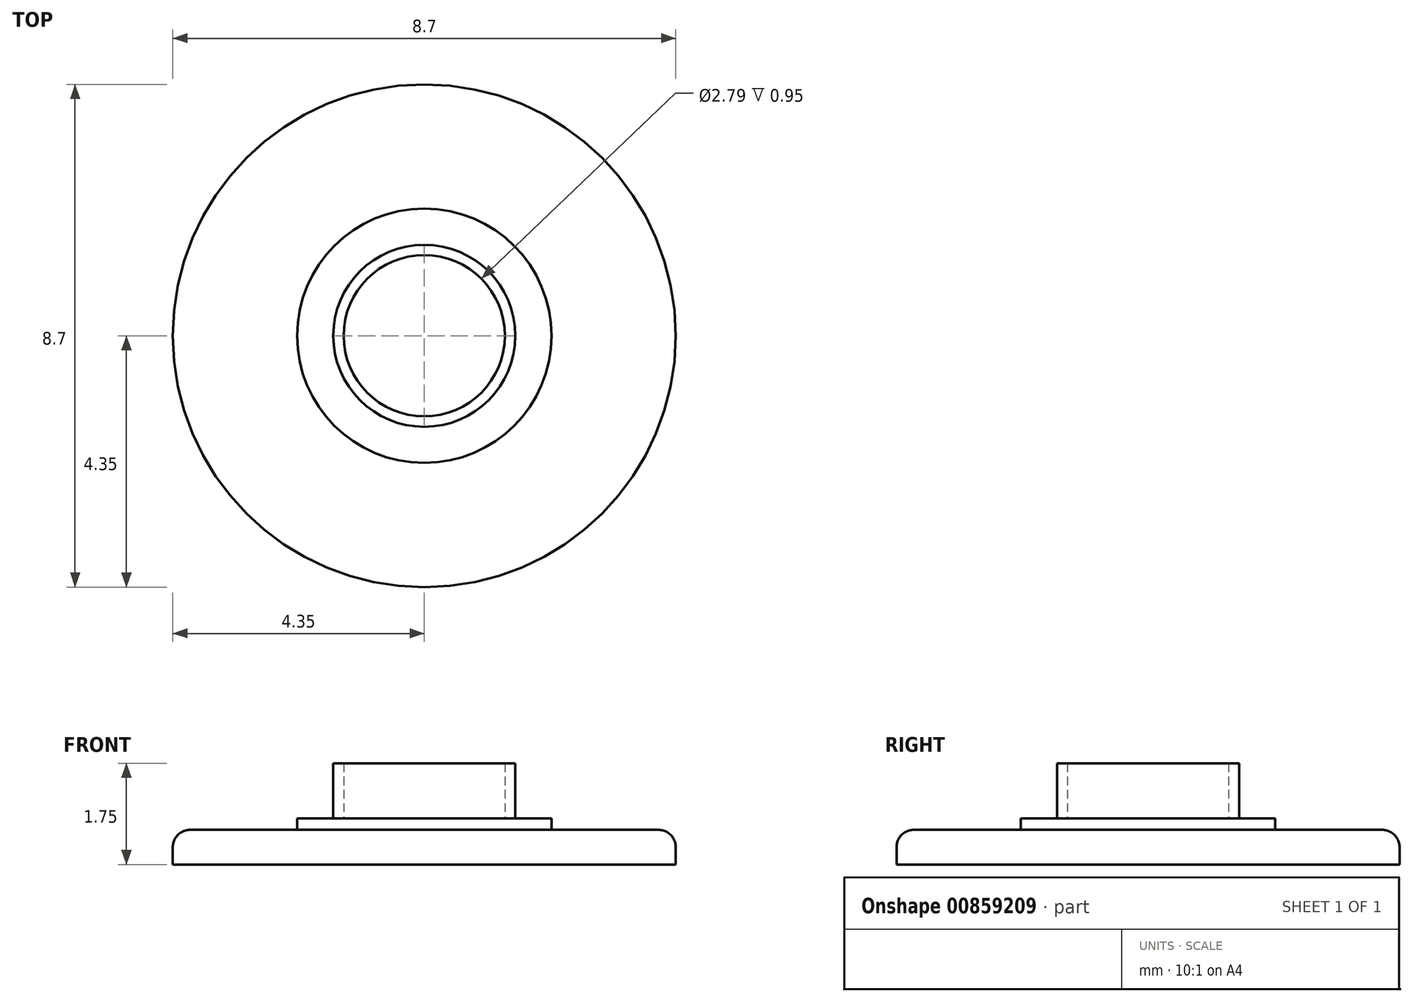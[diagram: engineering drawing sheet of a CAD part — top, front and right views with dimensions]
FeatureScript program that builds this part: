
annotation { "Feature Type Name" : "Feature", "Feature Type Description" : "" }
export const myFeature = defineFeature(function(context is Context, id is Id, definition is map)
    precondition{}
    {
        {
            var Q0;
            Q0=qCreatedBy(makeId("Top.planeOp"),FACE);
            var sketch = newSketch(context, id + "F0", { "sketchPlane" : qUnion([Q0])});
            skCircle(sketch, "E0", {"center": v(0, 0) * mm, "radius": 4.35 * mm});
            skSolve(sketch);
        }
        {
            var Q0;
            Q0 = qSketchRegion(id + "F0", true);
            extrude(context, id + "F1", {"entities" : qUnion([Q0]), "depth" : 0.6 * mm, "offsetDistance" : 25 * mm});
        }
        {
            var Q0;
            Q0=makeQuery(id+"F1.opExtrude","CAP_FACE",FACE,{"disambiguationData":[OSD([sQuery(id+"F0.wireOp",EDGE,"E0")])],"isStart":false});
            var sketch = newSketch(context, id + "F2", { "sketchPlane" : qUnion([Q0])});
            skCircle(sketch, "E1", {"center": v(0, 0) * mm, "radius": 2.2 * mm});
            skSolve(sketch);
        }
        {
            var Q0;
            Q0 = qSketchRegion(id + "F2", true);
            extrude(context, id + "F3", {"entities" : qUnion([Q0]), "operationType" : NewBodyOperationType.ADD, "depth" : 0.2 * mm, "offsetDistance" : 25 * mm});
        }
        {
            var Q0;
            Q0=makeQuery(id+"F3.opExtrude","CAP_FACE",FACE,{"disambiguationData":[OSD([sQuery(id+"F2.wireOp",EDGE,"E1")])],"isStart":false});
            var sketch = newSketch(context, id + "F4", { "sketchPlane" : qUnion([Q0])});
            skCircle(sketch, "E2", {"center": v(0, 0) * mm, "radius": 1.57 * mm});
            skCircle(sketch, "E3.0", {"center": v(0, 0) * mm, "radius": 1.4 * mm});
            skSolve(sketch);
        }
        {
            var Q0;
            Q0=makeQuery(id+"F4.imprint","IMPRINT",FACE,{"disambiguationData":[TD([[makeQuery(id+"F4.imprint","IMPRINT",EDGE,{"derivedFrom":sQuery(id+"F4.wireOp",EDGE,"E2")}),1.0]])]});
            extrude(context, id + "F5", {"entities" : qUnion([Q0]), "operationType" : NewBodyOperationType.ADD, "depth" : 0.95 * mm, "offsetDistance" : 25 * mm});
        }
        {
            var Q0;
            Q0=makeQuery(id+"F1.opExtrude","CAP_EDGE",EDGE,{"disambiguationData":[OSD([sQuery(id+"F0.wireOp",EDGE,"E0")])],"isStart":false});
            fillet(context, id + "F6", {"entities" : qUnion([Q0]), "radius" : 0.3 * mm, "tangentPropagation" : true, "allowEdgeOverflow" : false});
        }
    });
